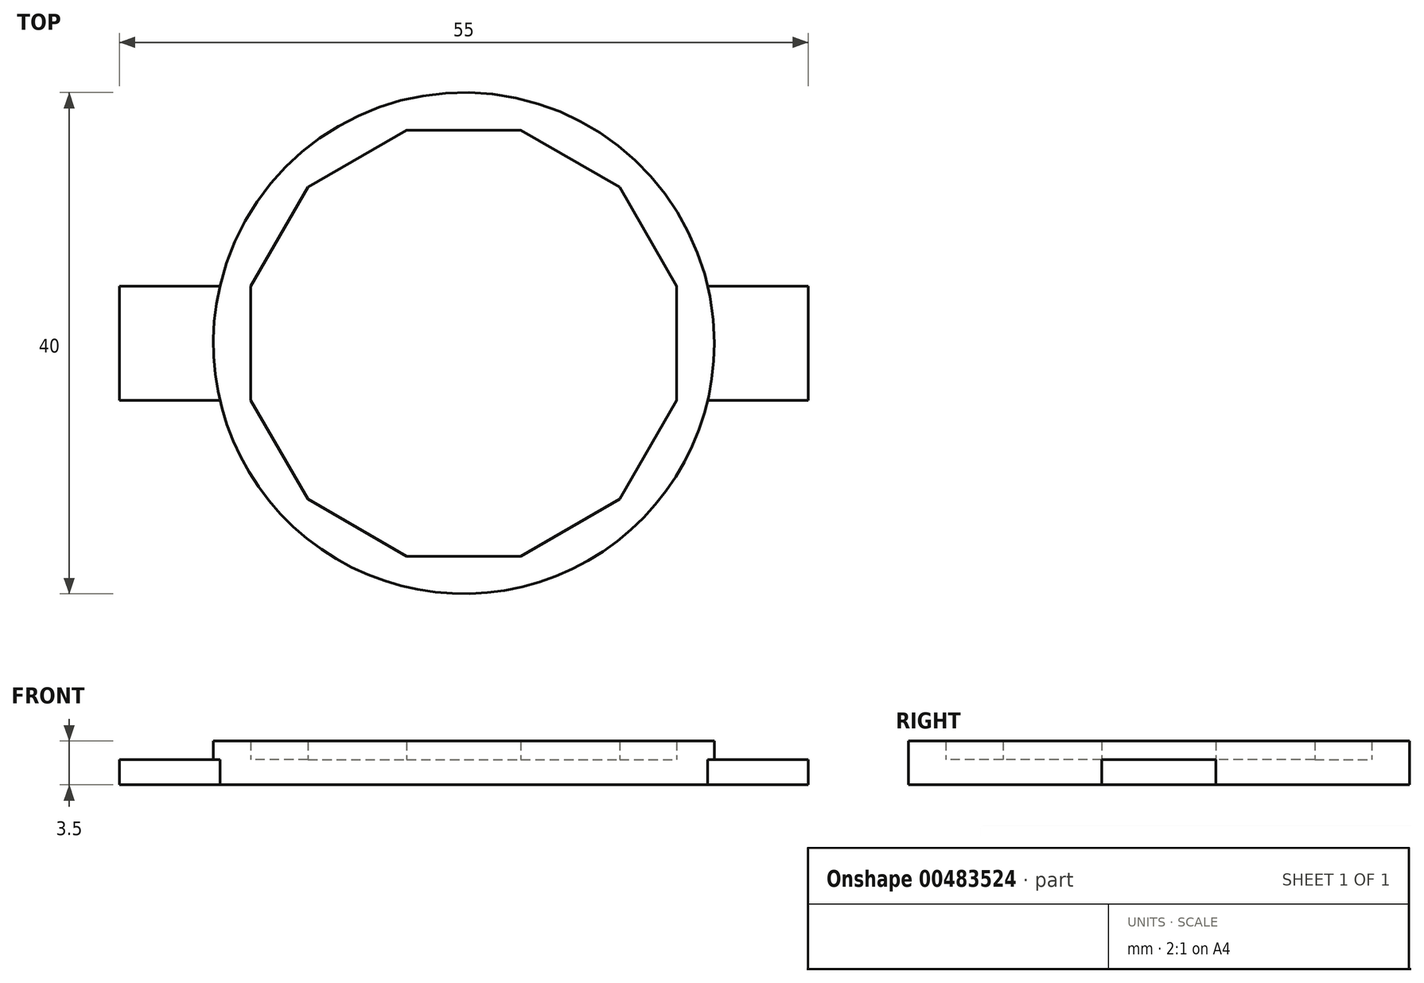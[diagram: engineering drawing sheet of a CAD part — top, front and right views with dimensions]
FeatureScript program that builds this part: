
annotation { "Feature Type Name" : "Feature", "Feature Type Description" : "" }
export const myFeature = defineFeature(function(context is Context, id is Id, definition is map)
    precondition{}
    {
        {
            var Q0;
            Q0=qCreatedBy(makeId("Top.planeOp"),FACE);
            var sketch = newSketch(context, id + "F0", { "sketchPlane" : qUnion([Q0])});
            skCircle(sketch, "E0.cCircle", {"center": v(0, 0) * mm, "radius": 17 * mm, "construction": true});
            skLineSegment(sketch, "E0.0", {"start": v(-4.56, 17) * mm, "end": v(4.56, 17) * mm});
            skLineSegment(sketch, "E0.1", {"start": v(4.56, 17) * mm, "end": v(12.44, 12.44) * mm});
            skLineSegment(sketch, "E0.2", {"start": v(12.44, 12.44) * mm, "end": v(17, 4.56) * mm});
            skLineSegment(sketch, "E0.3", {"start": v(17, 4.56) * mm, "end": v(17, -4.56) * mm});
            skLineSegment(sketch, "E0.4", {"start": v(17, -4.56) * mm, "end": v(12.44, -12.44) * mm});
            skLineSegment(sketch, "E0.5", {"start": v(12.44, -12.44) * mm, "end": v(4.56, -17) * mm});
            skLineSegment(sketch, "E0.6", {"start": v(4.56, -17) * mm, "end": v(-4.56, -17) * mm});
            skLineSegment(sketch, "E0.7", {"start": v(-4.56, -17) * mm, "end": v(-12.44, -12.44) * mm});
            skLineSegment(sketch, "E0.8", {"start": v(-12.44, -12.44) * mm, "end": v(-17, -4.56) * mm});
            skLineSegment(sketch, "E0.9", {"start": v(-17, -4.56) * mm, "end": v(-17, 4.56) * mm});
            skLineSegment(sketch, "E0.10", {"start": v(-17, 4.56) * mm, "end": v(-12.44, 12.44) * mm});
            skLineSegment(sketch, "E0.11", {"start": v(-12.44, 12.44) * mm, "end": v(-4.56, 17) * mm});
            skPoint(sketch, "E0.0.midPoint", {"position": v(0, 17) * mm});
            skCircle(sketch, "E1", {"center": v(0, 0) * mm, "radius": 20 * mm});
            skSolve(sketch);
        }
        {
            var Q0;
            Q0=makeQuery(id+"F0.imprint","IMPRINT",FACE,{"disambiguationData":[TD([[makeQuery(id+"F0.imprint","IMPRINT",EDGE,{"derivedFrom":sQuery(id+"F0.wireOp",EDGE,"E0.0")}),1.0]])]});
            extrude(context, id + "F1", {"entities" : qUnion([Q0]), "depth" : 3.5 * mm});
        }
        {
            var Q0;
            Q0=makeQuery(id+"F1.opExtrude","CAP_FACE",FACE,{"disambiguationData":[OSD([sQuery(id+"F0.wireOp",EDGE,"E0.0"),sQuery(id+"F0.wireOp",EDGE,"E0.1"),sQuery(id+"F0.wireOp",EDGE,"E0.2"),sQuery(id+"F0.wireOp",EDGE,"E0.3"),sQuery(id+"F0.wireOp",EDGE,"E0.4"),sQuery(id+"F0.wireOp",EDGE,"E0.5"),sQuery(id+"F0.wireOp",EDGE,"E0.6"),sQuery(id+"F0.wireOp",EDGE,"E0.7"),sQuery(id+"F0.wireOp",EDGE,"E0.8"),sQuery(id+"F0.wireOp",EDGE,"E0.9"),sQuery(id+"F0.wireOp",EDGE,"E0.10"),sQuery(id+"F0.wireOp",EDGE,"E0.11"),sQuery(id+"F0.wireOp",EDGE,"E1")])],"isStart":false});
            var sketch = newSketch(context, id + "F2", { "sketchPlane" : qUnion([Q0])});
            skLineSegment(sketch, "E2.bottom", {"start": v(-19.47, -4.56) * mm, "end": v(-17, -4.56) * mm});
            skLineSegment(sketch, "E2.top", {"start": v(-19.47, 4.56) * mm, "end": v(-17, 4.56) * mm});
            skLineSegment(sketch, "E2.left", {"start": v(-19.47, -4.56) * mm, "end": v(-19.47, 4.56) * mm});
            skLineSegment(sketch, "E2.right", {"start": v(-17, -4.56) * mm, "end": v(-17, 4.56) * mm});
            skLineSegment(sketch, "E3.bottom", {"start": v(17, 4.56) * mm, "end": v(19.47, 4.56) * mm});
            skLineSegment(sketch, "E3.top", {"start": v(17, -4.56) * mm, "end": v(19.47, -4.56) * mm});
            skLineSegment(sketch, "E3.left", {"start": v(17, 4.56) * mm, "end": v(17, -4.56) * mm});
            skLineSegment(sketch, "E3.right", {"start": v(19.47, 4.56) * mm, "end": v(19.47, -4.56) * mm});
            skSolve(sketch);
        }
        {
            var Q0;
            Q0=qCreatedBy(makeId("Top.planeOp"),FACE);
            var sketch = newSketch(context, id + "F3", { "sketchPlane" : qUnion([Q0])});
            skCircle(sketch, "E4", {"center": v(0, 0) * mm, "radius": 20 * mm});
            skSolve(sketch);
        }
        {
            var Q0;
            Q0 = qSketchRegion(id + "F3", true);
            extrude(context, id + "F4", {"entities" : qUnion([Q0]), "operationType" : NewBodyOperationType.ADD, "depth" : 2 * mm});
        }
        {
            var Q0;
            Q0=qCreatedBy(makeId("Top.planeOp"),FACE);
            var sketch = newSketch(context, id + "F5", { "sketchPlane" : qUnion([Q0])});
            skLineSegment(sketch, "E5.bottom", {"start": v(27.5, 4.56) * mm, "end": v(-27.5, 4.56) * mm});
            skLineSegment(sketch, "E5.top", {"start": v(27.5, -4.56) * mm, "end": v(-27.5, -4.56) * mm});
            skLineSegment(sketch, "E5.left", {"start": v(27.5, 4.56) * mm, "end": v(27.5, -4.56) * mm});
            skLineSegment(sketch, "E5.right", {"start": v(-27.5, 4.56) * mm, "end": v(-27.5, -4.56) * mm});
            skPoint(sketch, "E5.middle", {"position": v(0, 0) * mm});
            skSolve(sketch);
        }
        {
            var Q0;
            Q0=makeQuery(id+"F5.imprint","IMPRINT",FACE,{"disambiguationData":[TD([[makeQuery(id+"F5.imprint","IMPRINT",EDGE,{"derivedFrom":sQuery(id+"F5.wireOp",EDGE,"E5.bottom")}),1.0]])]});
            extrude(context, id + "F6", {"entities" : qUnion([Q0]), "operationType" : NewBodyOperationType.ADD, "depth" : 2 * mm});
        }
    });
